# Revit family: Sink-Single-Clark-Monaco-Overmount
name_source: partatom
category: Plumbing Fixtures
revit_build: Autodesk Revit MEP 2012 (Build: 20110916_2132(x64)
units: mm (PartAtom-declared; Revit-internal decimal feet)

## types (1)
- Standard
    Assembly Code = D2010410
    CW Connection = No
    Cost = 399 $
    Default Elevation = 0 mm  [stored 0 ft]
    Description = MONACO SINGLE BOWL OVERMOUNT
    HW Connection = No
    Keynote = SK
    Manufacturer = Clark
    Material_ANZRS = Metal-Chrome-Caroma
    Model = EVB
    PlumbingMaterial_ANZRS = PVC-White-Caroma
    Tap_Cutout_Required = No
    Type Comments = Includes timber board, small colander, stainless steel draining basket and basket wastes
    URL = http://www.clark.com.au
    Vent Connection = No
    WFU = 2
    Waste = Metal-Chrome-Caroma
    Waste Connection = Yes

note: [stored X ft] marks values corroborated as IEEE doubles in the binary element streams (Revit-internal decimal feet)

## geometry (parser evidence)
native form markers: Blend x6, Sweep x7
no freeform markers — native parametric forms only
